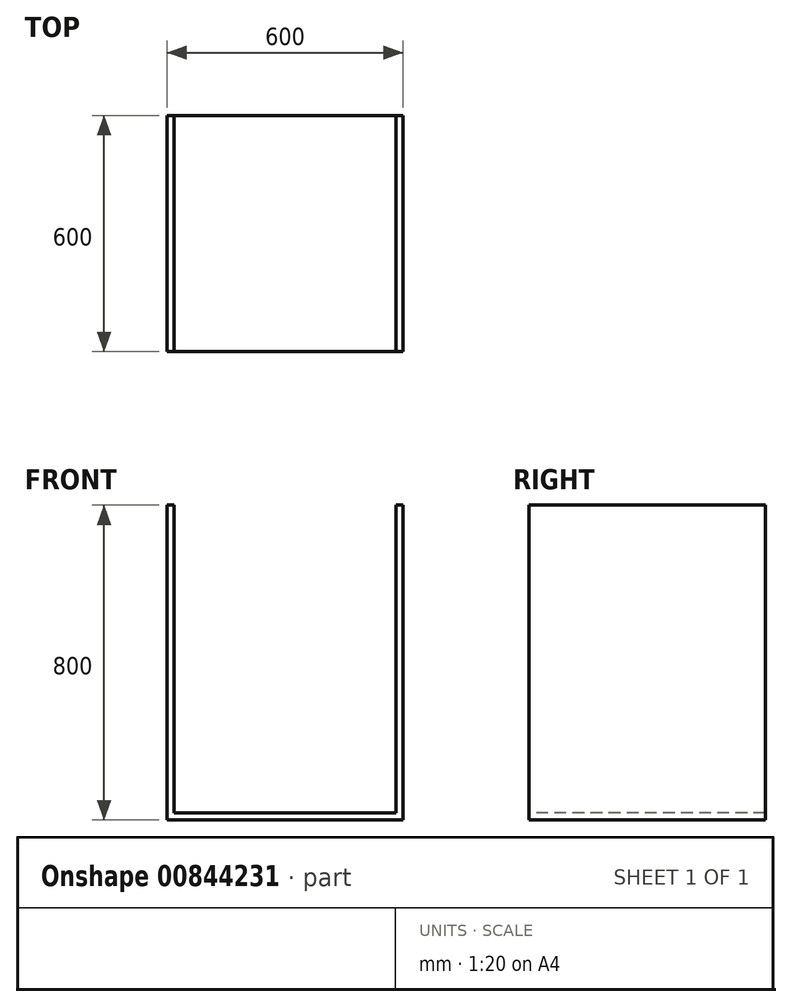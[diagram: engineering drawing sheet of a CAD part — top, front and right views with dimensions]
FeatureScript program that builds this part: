
annotation { "Feature Type Name" : "Feature", "Feature Type Description" : "" }
export const myFeature = defineFeature(function(context is Context, id is Id, definition is map)
    precondition{}
    {
        {
            var Q0;
            Q0=qCreatedBy(makeId("Top.planeOp"),FACE);
            var sketch = newSketch(context, id + "F0", { "sketchPlane" : qUnion([Q0])});
            skLineSegment(sketch, "E0.bottom", {"start": v(0, 0) * mm, "end": v(50.36, 0) * mm});
            skLineSegment(sketch, "E0.top", {"start": v(0, -47.1) * mm, "end": v(50.36, -47.1) * mm});
            skLineSegment(sketch, "E0.left", {"start": v(0, 0) * mm, "end": v(0, -47.1) * mm});
            skLineSegment(sketch, "E0.right", {"start": v(50.36, 0) * mm, "end": v(50.36, -47.1) * mm});
            skSolve(sketch);
        }
        {
            var Q0;
            Q0=makeQuery(id+"F0.imprint","IMPRINT",FACE,{"disambiguationData":[TD([[makeQuery(id+"F0.imprint","IMPRINT",EDGE,{"derivedFrom":sQuery(id+"F0.wireOp",EDGE,"E0.bottom")}),-1.0]])]});
            extrude(context, id + "F1", {"entities" : qUnion([Q0]), "depth" : 800 * mm, "offsetDistance" : 25 * mm});
        }
        {
            var Q0;
            Q0=makeQuery(id+"F1.opExtrude","SWEPT_FACE",FACE,{"disambiguationData":[OSD([sQuery(id+"F0.wireOp",EDGE,"E0.left")])]});
            extrude(context, id + "F2", {"entities" : qUnion([Q0]), "operationType" : NewBodyOperationType.ADD, "oppositeDirection" : true, "depth" : 600 * mm, "offsetDistance" : 25 * mm});
        }
        {
            var Q0;
            {var subQ0=sQuery(id+"F0.wireOp",EDGE,"E0.top");Q0=makeQuery(id+"F2.boolean.opBoolean","MERGE",FACE,{"derivedFrom":[makeQuery(id+"F1.opExtrude","SWEPT_FACE",FACE,{"disambiguationData":[OSD([subQ0])]}),makeQuery(id+"F2.opExtrude","SWEPT_FACE",FACE,{"disambiguationData":[OSD([subQ0,sQuery(id+"F0.wireOp",EDGE,"E0.left")])]})]});}
            extrude(context, id + "F3", {"entities" : qUnion([Q0]), "operationType" : NewBodyOperationType.ADD, "oppositeDirection" : true, "depth" : 600 * mm, "offsetDistance" : 25 * mm});
        }
        {
            var Q0;
            {var subQ0=sQuery(id+"F0.wireOp",EDGE,"E0.left");var subQ1=sQuery(id+"F0.wireOp",EDGE,"E0.top");Q0=makeQuery(id+"F3.boolean.opBoolean","MERGE",FACE,{"derivedFrom":[makeQuery(id+"F2.boolean.opBoolean","MERGE",FACE,{"derivedFrom":[makeQuery(id+"F1.opExtrude","CAP_FACE",FACE,{"disambiguationData":[OSD([sQuery(id+"F0.wireOp",EDGE,"E0.bottom"),subQ1,subQ0,sQuery(id+"F0.wireOp",EDGE,"E0.right")])],"isStart":false}),makeQuery(id+"F2.opExtrude","SWEPT_FACE",FACE,{"disambiguationData":[OSD([subQ0]),TDD([makeQuery(id+"F1.opExtrude","CAP_EDGE",EDGE,{"disambiguationData":[OSD([subQ0])],"isStart":false})])]})]}),makeQuery(id+"F3.opExtrude","SWEPT_FACE",FACE,{"disambiguationData":[OSD([subQ1,subQ0]),TDD([makeQuery(id+"F2.boolean.opBoolean","MERGE",EDGE,{"derivedFrom":[makeQuery(id+"F1.opExtrude","CAP_EDGE",EDGE,{"disambiguationData":[OSD([subQ1])],"isStart":false}),makeQuery(id+"F2.opExtrude","SWEPT_EDGE",EDGE,{"disambiguationData":[OSD([subQ1,subQ0]),TDD([makeQuery(id+"F1.opExtrude","CAP_VERTEX",VERTEX,{"disambiguationData":[OSD([subQ1,subQ0])],"isStart":false})])]})]})])]})]});}
            var Q1;
            {var subQ0=sQuery(id+"F0.wireOp",EDGE,"E0.top");Q1=makeQuery(id+"F2.boolean.opBoolean","MERGE",FACE,{"derivedFrom":[makeQuery(id+"F1.opExtrude","SWEPT_FACE",FACE,{"disambiguationData":[OSD([subQ0])]}),makeQuery(id+"F2.opExtrude","SWEPT_FACE",FACE,{"disambiguationData":[OSD([subQ0,sQuery(id+"F0.wireOp",EDGE,"E0.left")])]})]});}
            shell(context, id + "F4", {"entities" : qUnion([Q0, Q1]), "thickness" : 18 * mm});
        }
        {
            var Q0;
            {var subQ0=sQuery(id+"F0.wireOp",EDGE,"E0.left");var subQ1=sQuery(id+"F0.wireOp",EDGE,"E0.top");Q0=makeQuery(id+"F3.boolean.opBoolean","MERGE",FACE,{"derivedFrom":[makeQuery(id+"F2.boolean.opBoolean","MERGE",FACE,{"derivedFrom":[makeQuery(id+"F1.opExtrude","CAP_FACE",FACE,{"disambiguationData":[OSD([sQuery(id+"F0.wireOp",EDGE,"E0.bottom"),subQ1,subQ0,sQuery(id+"F0.wireOp",EDGE,"E0.right")])],"isStart":false}),makeQuery(id+"F2.opExtrude","SWEPT_FACE",FACE,{"disambiguationData":[OSD([subQ0]),TDD([makeQuery(id+"F1.opExtrude","CAP_EDGE",EDGE,{"disambiguationData":[OSD([subQ0])],"isStart":false})])]})]}),makeQuery(id+"F3.opExtrude","SWEPT_FACE",FACE,{"disambiguationData":[OSD([subQ1,subQ0]),TDD([makeQuery(id+"F2.boolean.opBoolean","MERGE",EDGE,{"derivedFrom":[makeQuery(id+"F1.opExtrude","CAP_EDGE",EDGE,{"disambiguationData":[OSD([subQ1])],"isStart":false}),makeQuery(id+"F2.opExtrude","SWEPT_EDGE",EDGE,{"disambiguationData":[OSD([subQ1,subQ0]),TDD([makeQuery(id+"F1.opExtrude","CAP_VERTEX",VERTEX,{"disambiguationData":[OSD([subQ1,subQ0])],"isStart":false})])]})]})])]})]});}
            extrude(context, id + "F5", {"entities" : qUnion([Q0]), "operationType" : NewBodyOperationType.ADD, "depth" : 80 * mm, "offsetDistance" : 25 * mm});
        }
        {
            var Q0;
            {var subQ0=sQuery(id+"F0.wireOp",EDGE,"E0.left");var subQ1=sQuery(id+"F0.wireOp",EDGE,"E0.top");Q0=makeQuery(id+"F5.boolean.opBoolean","MERGE",FACE,{"derivedFrom":[makeQuery(id+"F4.opShell","OFFSET_FACE",FACE,{"disambiguationData":[OSD([subQ1,subQ0]),TDD([makeQuery(id+"F3.opExtrude","CAP_FACE",FACE,{"disambiguationData":[OSD([subQ1,subQ0])],"isStart":false})])]}),makeQuery(id+"F5.opExtrude","SWEPT_FACE",FACE,{"disambiguationData":[OSD([subQ1,subQ0]),TDD([makeQuery(id+"F4.opShell","OFFSET_EDGE",EDGE,{"disambiguationData":[OSD([subQ1,subQ0]),TDD([makeQuery(id+"F3.opExtrude","CAP_EDGE",EDGE,{"disambiguationData":[OSD([subQ1,subQ0]),TDD([makeQuery(id+"F2.boolean.opBoolean","MERGE",EDGE,{"derivedFrom":[makeQuery(id+"F1.opExtrude","CAP_EDGE",EDGE,{"disambiguationData":[OSD([subQ1])],"isStart":false}),makeQuery(id+"F2.opExtrude","SWEPT_EDGE",EDGE,{"disambiguationData":[OSD([subQ1,subQ0]),TDD([makeQuery(id+"F1.opExtrude","CAP_VERTEX",VERTEX,{"disambiguationData":[OSD([subQ1,subQ0])],"isStart":false})])]})]})])],"isStart":false})])]})])]})]});}
            extrude(context, id + "F6", {"entities" : qUnion([Q0]), "operationType" : NewBodyOperationType.REMOVE, "oppositeDirection" : true, "depth" : 25 * mm, "offsetDistance" : 25 * mm});
        }
        {
            var Q0;
            {var subQ0=sQuery(id+"F0.wireOp",EDGE,"E0.left");var subQ1=sQuery(id+"F0.wireOp",EDGE,"E0.top");var subQ5=makeQuery(id+"F2.opExtrude","CAP_FACE",FACE,{"disambiguationData":[OSD([subQ0])],"isStart":false});Q0=makeQuery(id+"F6.boolean.opBoolean","SPLIT",FACE,{"disambiguationData":[TD([subQ5])],"derivedFrom":makeQuery(id+"F5.opExtrude","CAP_FACE",FACE,{"disambiguationData":[OSD([sQuery(id+"F0.wireOp",EDGE,"E0.bottom"),subQ1,subQ0,sQuery(id+"F0.wireOp",EDGE,"E0.right")])],"isStart":false})});}
            var Q1;
            {var subQ0=sQuery(id+"F0.wireOp",EDGE,"E0.left");var subQ1=sQuery(id+"F0.wireOp",EDGE,"E0.top");var subQ7=makeQuery(id+"F1.opExtrude","SWEPT_FACE",FACE,{"disambiguationData":[OSD([subQ0])]});Q1=makeQuery(id+"F6.boolean.opBoolean","SPLIT",FACE,{"disambiguationData":[TD([subQ7])],"derivedFrom":makeQuery(id+"F5.opExtrude","CAP_FACE",FACE,{"disambiguationData":[OSD([sQuery(id+"F0.wireOp",EDGE,"E0.bottom"),subQ1,subQ0,sQuery(id+"F0.wireOp",EDGE,"E0.right")])],"isStart":false})});}
            extrude(context, id + "F7", {"entities" : qUnion([Q0, Q1]), "operationType" : NewBodyOperationType.REMOVE, "oppositeDirection" : true, "depth" : 80 * mm, "offsetDistance" : 25 * mm});
        }
    });
